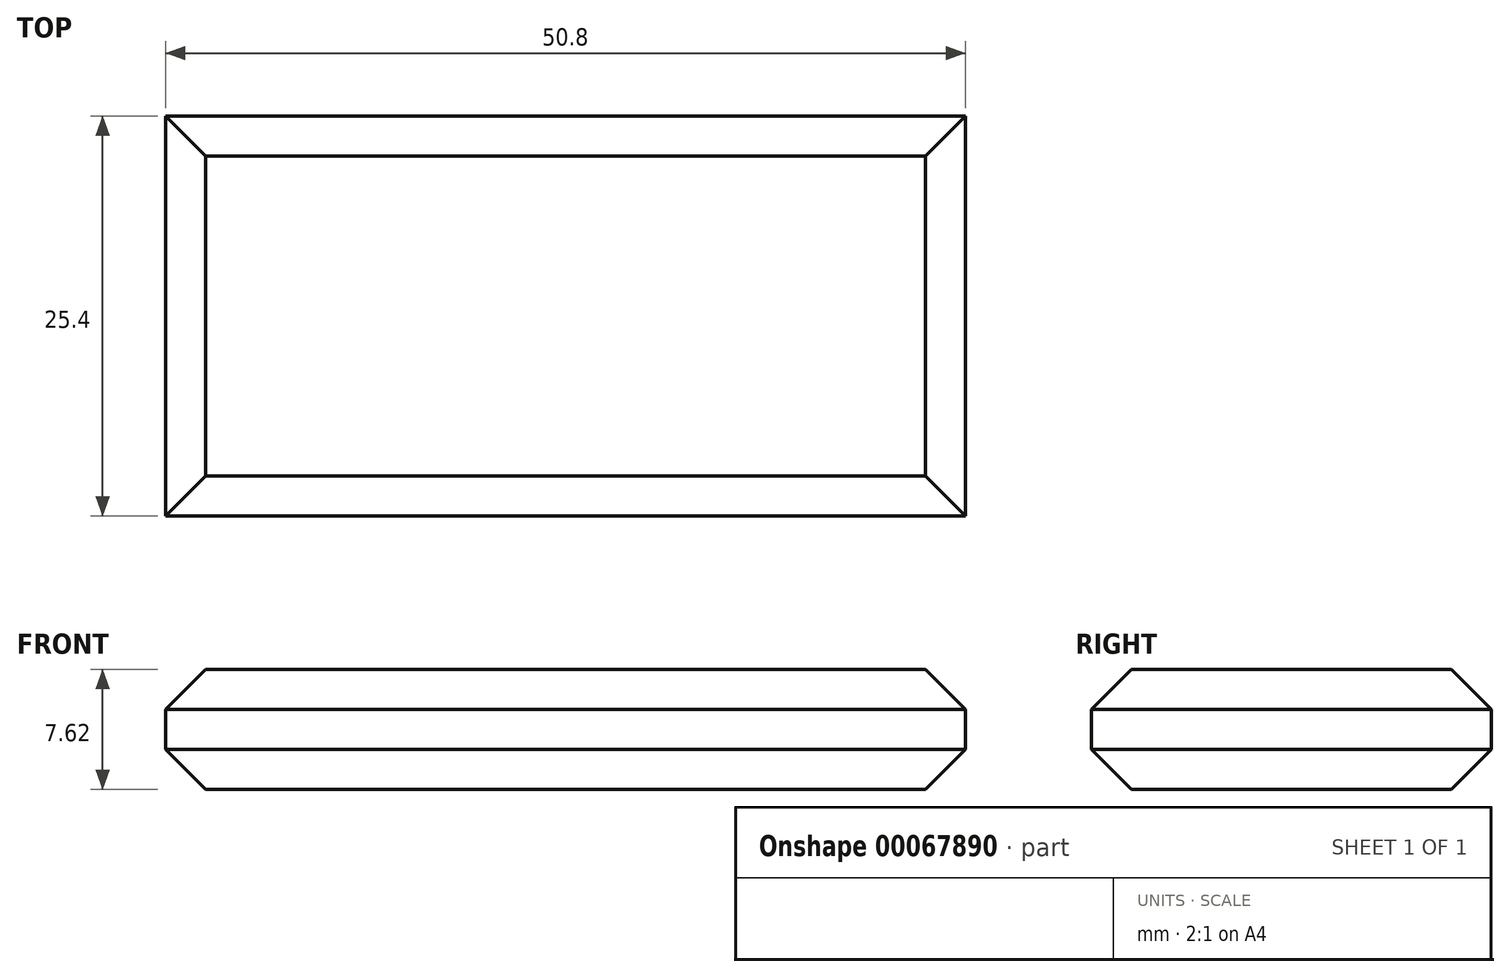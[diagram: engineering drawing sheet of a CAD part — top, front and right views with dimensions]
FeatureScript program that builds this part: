
annotation { "Feature Type Name" : "Feature", "Feature Type Description" : "" }
export const myFeature = defineFeature(function(context is Context, id is Id, definition is map)
    precondition{}
    {
        {
            var Q0;
            Q0=qCreatedBy(makeId("Top.planeOp"),FACE);
            var sketch = newSketch(context, id + "F0", { "sketchPlane" : qUnion([Q0])});
            skLineSegment(sketch, "E0.rect.bottom", {"start": v(-25.4, -12.7) * mm, "end": v(25.4, -12.7) * mm});
            skLineSegment(sketch, "E0.rect.top", {"start": v(-25.4, 12.7) * mm, "end": v(25.4, 12.7) * mm});
            skLineSegment(sketch, "E0.rect.left", {"start": v(-25.4, -12.7) * mm, "end": v(-25.4, 12.7) * mm});
            skLineSegment(sketch, "E0.rect.right", {"start": v(25.4, -12.7) * mm, "end": v(25.4, 12.7) * mm});
            skPoint(sketch, "E0.rect.middle", {"position": v(0, 0) * mm});
            skSolve(sketch);
        }
        {
            var Q0;
            Q0=makeQuery(id+"F0.imprint","IMPRINT",FACE,{"disambiguationData":[TD([[makeQuery(id+"F0.imprint","IMPRINT",EDGE,{"derivedFrom":sQuery(id+"F0.wireOp",EDGE,"E0.rect.bottom")}),1.0]])]});
            extrude(context, id + "F1", {"entities" : qUnion([Q0]), "depth" : 7.62 * mm});
        }
        {
            var Q0;
            Q0=makeQuery(id+"F1.opExtrude","CAP_EDGE",EDGE,{"disambiguationData":[OSD([sQuery(id+"F0.wireOp",EDGE,"E0.rect.left")])],"isStart":false});
            var Q1;
            Q1=makeQuery(id+"F1.opExtrude","CAP_EDGE",EDGE,{"disambiguationData":[OSD([sQuery(id+"F0.wireOp",EDGE,"E0.rect.bottom")])],"isStart":false});
            var Q2;
            Q2=makeQuery(id+"F1.opExtrude","CAP_EDGE",EDGE,{"disambiguationData":[OSD([sQuery(id+"F0.wireOp",EDGE,"E0.rect.top")])],"isStart":false});
            var Q3;
            Q3=makeQuery(id+"F1.opExtrude","CAP_EDGE",EDGE,{"disambiguationData":[OSD([sQuery(id+"F0.wireOp",EDGE,"E0.rect.right")])],"isStart":false});
            var Q4;
            Q4=makeQuery(id+"F1.opExtrude","CAP_EDGE",EDGE,{"disambiguationData":[OSD([sQuery(id+"F0.wireOp",EDGE,"E0.rect.bottom")])],"isStart":true});
            var Q5;
            Q5=makeQuery(id+"F1.opExtrude","CAP_EDGE",EDGE,{"disambiguationData":[OSD([sQuery(id+"F0.wireOp",EDGE,"E0.rect.top")])],"isStart":true});
            var Q6;
            Q6=makeQuery(id+"F1.opExtrude","CAP_EDGE",EDGE,{"disambiguationData":[OSD([sQuery(id+"F0.wireOp",EDGE,"E0.rect.left")])],"isStart":true});
            var Q7;
            Q7=makeQuery(id+"F1.opExtrude","CAP_EDGE",EDGE,{"disambiguationData":[OSD([sQuery(id+"F0.wireOp",EDGE,"E0.rect.right")])],"isStart":true});
            chamfer(context, id + "F2", {"entities" : qUnion([Q0, Q1, Q2, Q3, Q4, Q5, Q6, Q7]), "width" : 2.54 * mm, "tangentPropagation" : true});
        }
    });
